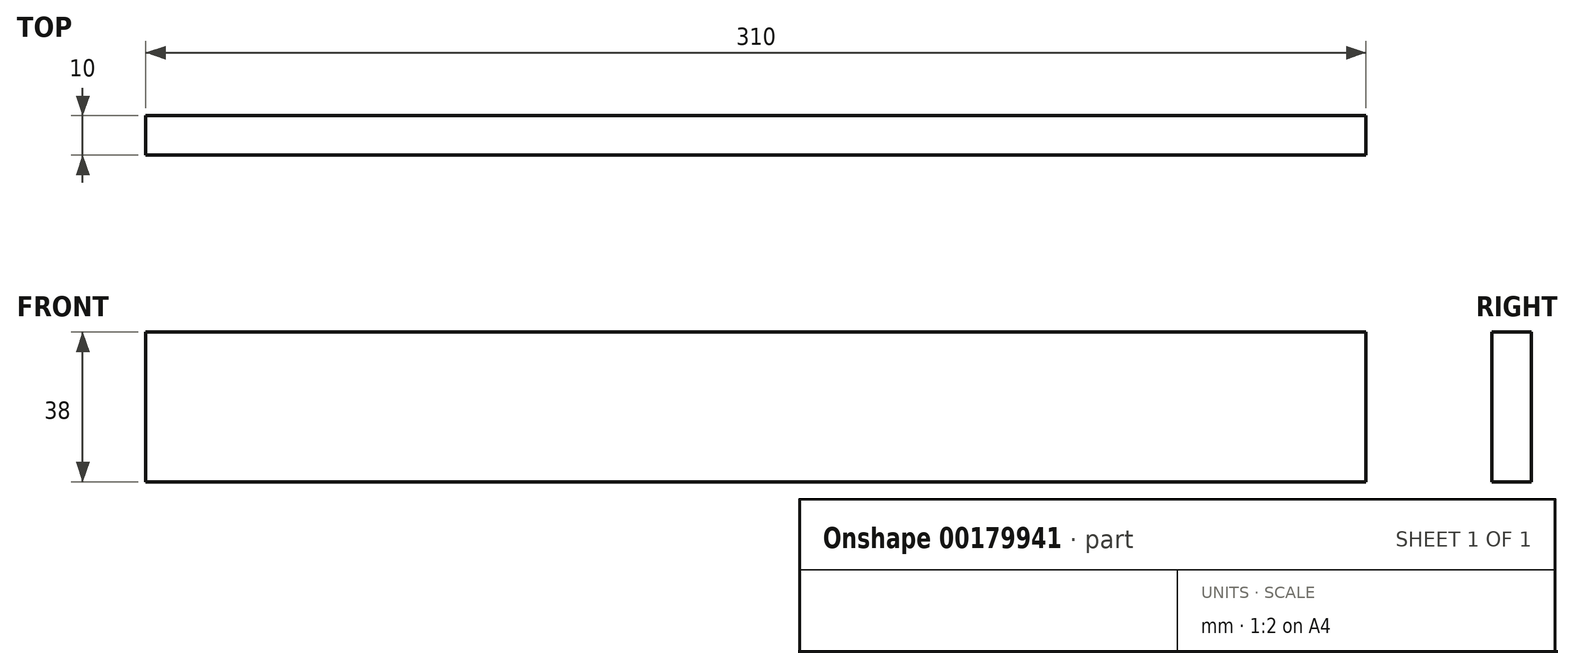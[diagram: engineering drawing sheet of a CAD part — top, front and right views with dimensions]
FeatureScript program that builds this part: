
annotation { "Feature Type Name" : "Feature", "Feature Type Description" : "" }
export const myFeature = defineFeature(function(context is Context, id is Id, definition is map)
    precondition{}
    {
        {
            var Q0;
            Q0=qCreatedBy(makeId("Front.planeOp"),FACE);
            var sketch = newSketch(context, id + "F0", { "sketchPlane" : qUnion([Q0])});
            skLineSegment(sketch, "E0.bottom", {"start": v(0, 0) * mm, "end": v(310, 0) * mm});
            skLineSegment(sketch, "E0.top", {"start": v(0, 38) * mm, "end": v(310, 38) * mm});
            skLineSegment(sketch, "E0.left", {"start": v(0, 0) * mm, "end": v(0, 38) * mm});
            skLineSegment(sketch, "E0.right", {"start": v(310, 0) * mm, "end": v(310, 38) * mm});
            skSolve(sketch);
        }
        {
            var Q0;
            Q0=qSketchRegion(id+"F0",true);
            extrude(context, id + "F1", {"entities" : qUnion([Q0]), "depth" : 10 * mm});
        }
    });
